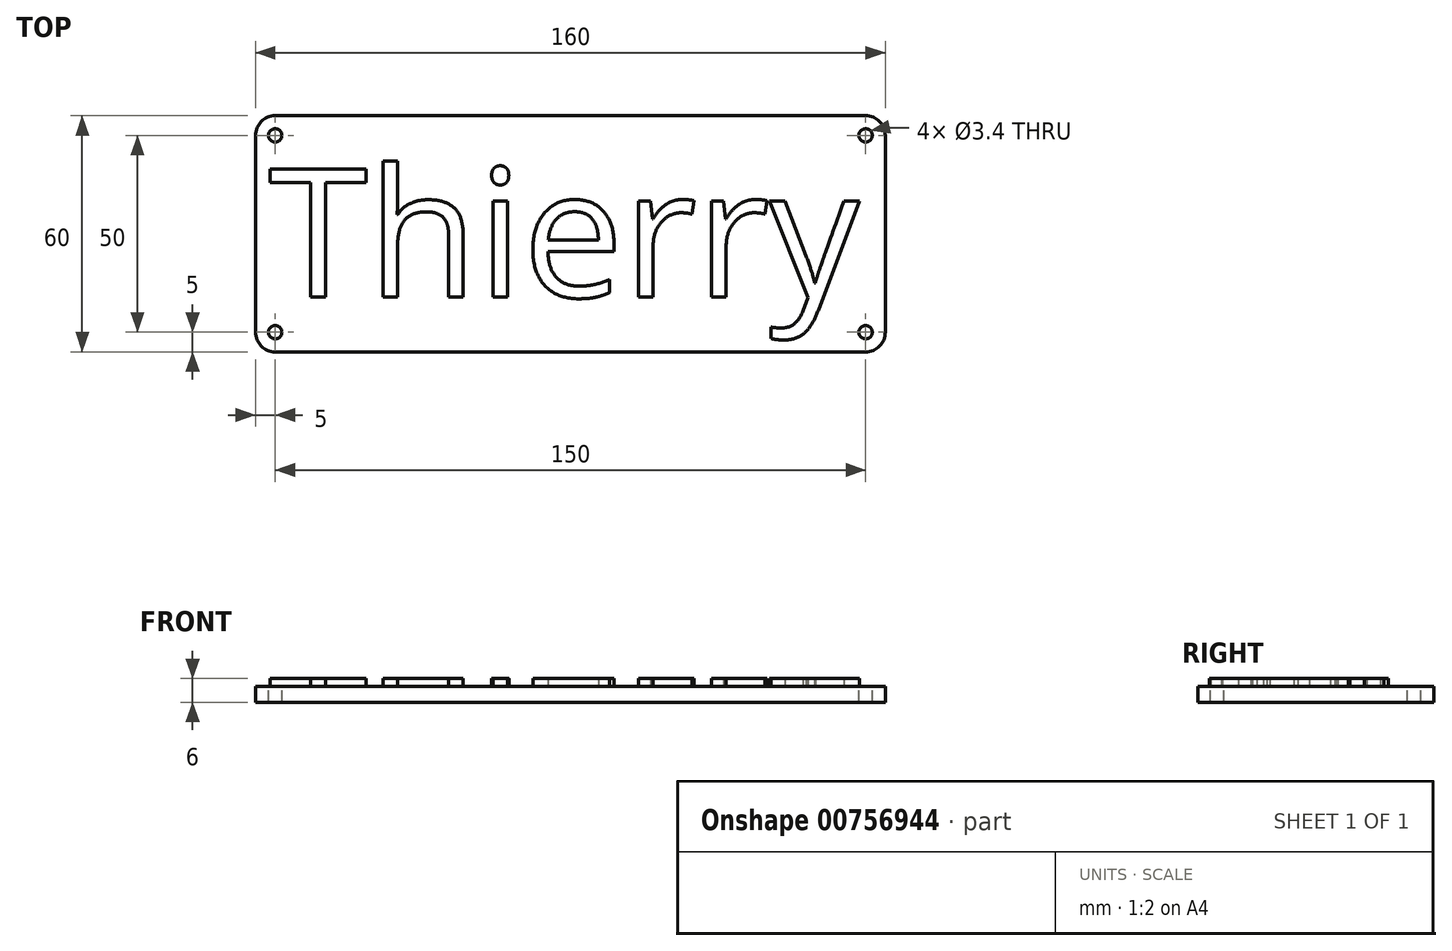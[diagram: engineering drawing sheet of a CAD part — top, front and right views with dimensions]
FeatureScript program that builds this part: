
annotation { "Feature Type Name" : "Feature", "Feature Type Description" : "" }
export const myFeature = defineFeature(function(context is Context, id is Id, definition is map)
    precondition{}
    {
        {
            var Q0;
            Q0=qCreatedBy(makeId("Top.planeOp"),FACE);
            var sketch = newSketch(context, id + "F0", { "sketchPlane" : qUnion([Q0])});
            skLineSegment(sketch, "E0.bottom", {"start": v(80, 30) * mm, "end": v(-80, 30) * mm});
            skLineSegment(sketch, "E0.top", {"start": v(80, -30) * mm, "end": v(-80, -30) * mm});
            skLineSegment(sketch, "E0.left", {"start": v(80, 30) * mm, "end": v(80, -30) * mm});
            skLineSegment(sketch, "E0.right", {"start": v(-80, 30) * mm, "end": v(-80, -30) * mm});
            skPoint(sketch, "E0.middle", {"position": v(0, 0) * mm});
            skSolve(sketch);
        }
        {
            var Q0;
            Q0=makeQuery(id+"F0.imprint","IMPRINT",FACE,{"disambiguationData":[TD([[makeQuery(id+"F0.imprint","IMPRINT",EDGE,{"derivedFrom":sQuery(id+"F0.wireOp",EDGE,"E0.bottom")}),1.0]])]});
            extrude(context, id + "F1", {"entities" : qUnion([Q0]), "depth" : 4 * mm, "offsetDistance" : 25 * mm});
        }
        {
            var Q0;
            Q0=makeQuery(id+"F1.opExtrude","SWEPT_EDGE",EDGE,{"disambiguationData":[OSD([sQuery(id+"F0.wireOp",EDGE,"E0.top"),sQuery(id+"F0.wireOp",EDGE,"E0.left")])]});
            var Q1;
            Q1=makeQuery(id+"F1.opExtrude","SWEPT_EDGE",EDGE,{"disambiguationData":[OSD([sQuery(id+"F0.wireOp",EDGE,"E0.bottom"),sQuery(id+"F0.wireOp",EDGE,"E0.left")])]});
            var Q2;
            Q2=makeQuery(id+"F1.opExtrude","SWEPT_EDGE",EDGE,{"disambiguationData":[OSD([sQuery(id+"F0.wireOp",EDGE,"E0.top"),sQuery(id+"F0.wireOp",EDGE,"E0.right")])]});
            var Q3;
            Q3=makeQuery(id+"F1.opExtrude","SWEPT_EDGE",EDGE,{"disambiguationData":[OSD([sQuery(id+"F0.wireOp",EDGE,"E0.bottom"),sQuery(id+"F0.wireOp",EDGE,"E0.right")])]});
            fillet(context, id + "F2", {"entities" : qUnion([Q0, Q1, Q2, Q3]), "radius" : 5 * mm, "tangentPropagation" : true, "allowEdgeOverflow" : false});
        }
        {
            var Q0;
            Q0=makeQuery(id+"F1.opExtrude","CAP_FACE",FACE,{"disambiguationData":[OSD([sQuery(id+"F0.wireOp",EDGE,"E0.bottom"),sQuery(id+"F0.wireOp",EDGE,"E0.top"),sQuery(id+"F0.wireOp",EDGE,"E0.left"),sQuery(id+"F0.wireOp",EDGE,"E0.right")])],"isStart":false});
            var sketch = newSketch(context, id + "F3", { "sketchPlane" : qUnion([Q0])});
            skPoint(sketch, "E1", {"position": v(75, 25) * mm});
            skPoint(sketch, "E2", {"position": v(-75, 25) * mm});
            skPoint(sketch, "E3", {"position": v(-75, -25) * mm});
            skPoint(sketch, "E4", {"position": v(75, -25) * mm});
            skSolve(sketch);
        }
        {
            var Q0;
            Q0=sQuery(id+"F3.wireOp",VERTEX,"E1");
            var Q1;
            Q1=sQuery(id+"F3.wireOp",VERTEX,"E4");
            var Q2;
            Q2=sQuery(id+"F3.wireOp",VERTEX,"E3");
            var Q3;
            Q3=sQuery(id+"F3.wireOp",VERTEX,"E2");
            var Q4;
            Q4=makeQuery(id+"F1.opExtrude","SWEPT_BODY",BODY,{"disambiguationData":[OSD([sQuery(id+"F0.wireOp",EDGE,"E0.bottom"),sQuery(id+"F0.wireOp",EDGE,"E0.top"),sQuery(id+"F0.wireOp",EDGE,"E0.left"),sQuery(id+"F0.wireOp",EDGE,"E0.right")])]});
            hole(context, id + "F4", {"style" : HoleStyle.SIMPLE, "endStyle" : HoleEndStyle.THROUGH, "holeDiameter" : 3.4 * mm, "majorDiameter" : 5 * mm, "isTappedThrough" : true, "tappedDepth" : 12 * mm, "tapClearance" : 3, "locations" : qUnion([Q0, Q1, Q2, Q3]), "scope" : qUnion([Q4])});
        }
        {
            var Q0;
            Q0=makeQuery(id+"F1.opExtrude","CAP_FACE",FACE,{"disambiguationData":[OSD([sQuery(id+"F0.wireOp",EDGE,"E0.bottom"),sQuery(id+"F0.wireOp",EDGE,"E0.top"),sQuery(id+"F0.wireOp",EDGE,"E0.left"),sQuery(id+"F0.wireOp",EDGE,"E0.right")])],"isStart":false});
            var sketch = newSketch(context, id + "F5", { "sketchPlane" : qUnion([Q0])});
            skText(sketch, "E5", { "text": "Thierry\n", "fontName": "OpenSans-Regular.ttf"});
            const initialGuessF5  = {"E5": [-0.07666, -0.01607, 1, 0, 0.03274]};
            skSetInitialGuess(sketch, initialGuessF5);
            skSolve(sketch);
        }
        {
            var Q0;
            Q0 = qSketchRegion(id + "F5", true);
            extrude(context, id + "F6", {"entities" : qUnion([Q0]), "operationType" : NewBodyOperationType.ADD, "depth" : 2 * mm, "offsetDistance" : 25 * mm});
        }
    });
